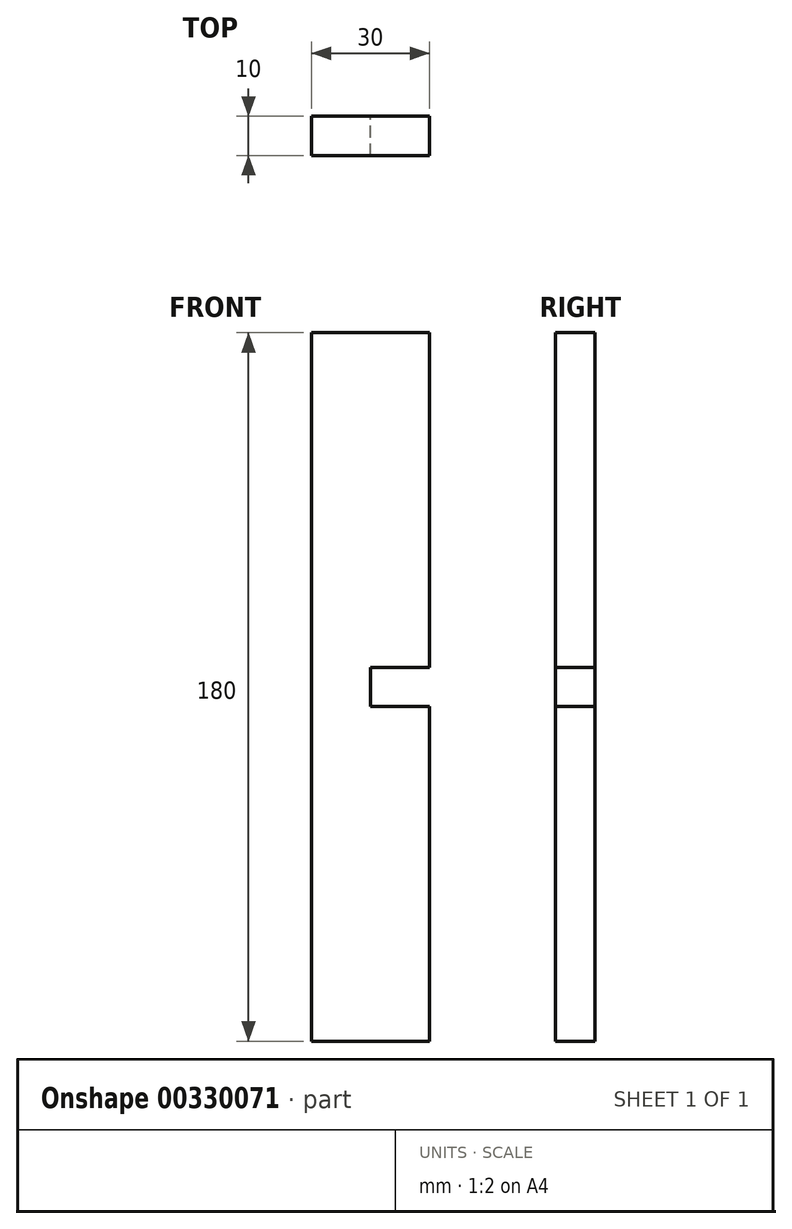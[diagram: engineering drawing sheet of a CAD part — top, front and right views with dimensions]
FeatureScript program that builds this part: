
annotation { "Feature Type Name" : "Feature", "Feature Type Description" : "" }
export const myFeature = defineFeature(function(context is Context, id is Id, definition is map)
    precondition{}
    {
        {
            var Q0;
            Q0=qCreatedBy(makeId("Front.planeOp"),FACE);
            var sketch = newSketch(context, id + "F0", { "sketchPlane" : qUnion([Q0])});
            skLineSegment(sketch, "E0.bottom", {"start": v(-50.87, -68.37) * mm, "end": v(-80.87, -68.37) * mm});
            skLineSegment(sketch, "E0.top", {"start": v(-50.87, 111.63) * mm, "end": v(-80.87, 111.63) * mm});
            skLineSegment(sketch, "E0.left", {"start": v(-50.87, -68.37) * mm, "end": v(-50.87, 16.63) * mm});
            skLineSegment(sketch, "E0.right", {"start": v(-80.87, -68.37) * mm, "end": v(-80.87, 111.63) * mm});
            skLineSegment(sketch, "E1", {"start": v(-65.87, 26.63) * mm, "end": v(-50.87, 26.63) * mm});
            skLineSegment(sketch, "E2", {"start": v(-65.87, 16.63) * mm, "end": v(-50.87, 16.63) * mm});
            skLineSegment(sketch, "E3", {"start": v(-65.87, 26.63) * mm, "end": v(-65.87, 16.63) * mm});
            skLineSegment(sketch, "E4.trimOffspring", {"start": v(-50.87, 26.63) * mm, "end": v(-50.87, 111.63) * mm});
            skSolve(sketch);
        }
        {
            var Q0;
            Q0 = qSketchRegion(id + "F0", true);
            extrude(context, id + "F1", {"entities" : qUnion([Q0]), "depth" : 10 * mm, "offsetDistance" : 25 * mm});
        }
    });
